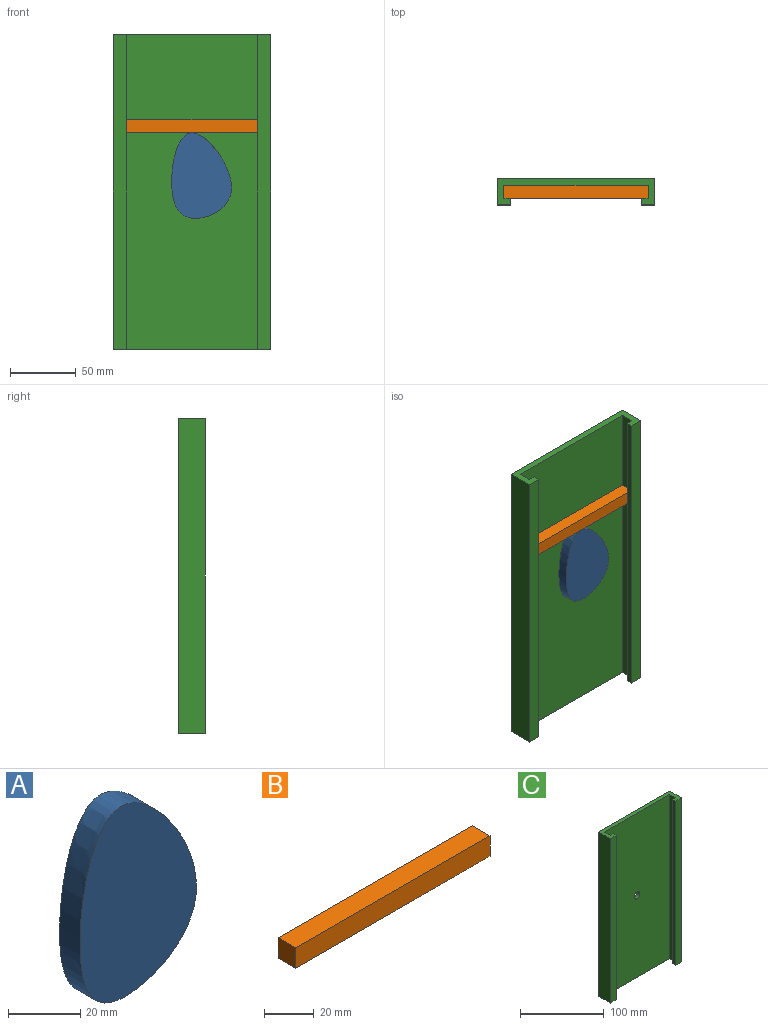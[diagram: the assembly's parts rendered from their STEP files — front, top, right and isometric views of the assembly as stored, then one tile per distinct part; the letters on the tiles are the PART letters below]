
ASSEMBLY  parts=3 mates=2
PART A: 5 faces, bbox 51x15x69 mm
  f0: plane 10x10mm, normal (0,1,0), area 78.5mm2, adj f1
  f1: cylinder r=5mm len=10mm, axis (0,-1,0), area 219.9mm2, adj f0,f4
  f2: extruded ~65.1x45.46mm, area 1405.8mm2, adj f3,f4
  f3: plane 69.02x51.05mm, normal (0,-1,0), area 2271.9mm2, adj f2
  f4: plane 69.02x51.05mm, normal (0,1,0), area 2193.4mm2, adj f1,f2
PART B: 6 faces, bbox 110x10x10 mm
  f0: plane 10x10mm, normal (1,0,0), area 100mm2, adj f1,f2,f4,f5
  f1: plane 110x10mm, normal (0,0,1), area 1100mm2, adj f0,f3,f4,f5
  f2: plane 110x10mm, normal (0,0,-1), area 1100mm2, adj f0,f3,f4,f5
  f3: plane 10x10mm, normal (-1,0,0), area 100mm2, adj f1,f2,f4,f5
  f4: plane 110x10mm, normal (0,1,0), area 1100mm2, adj f0,f1,f2,f3
  f5: plane 110x10mm, normal (0,-1,0), area 1100mm2, adj f0,f1,f2,f3
PART C: 15 faces, bbox 120x20x240 mm
  f0: plane 240x5mm, normal (1,0,0), area 1200mm2, adj f1,f3,f8,f13
  f1: plane 120x20mm, normal (0,0,-1), area 800mm2, adj f0,f2,f4,f5,f6,f7,f8,f9
  f2: plane 240x5mm, normal (-1,0,0), area 1200mm2, adj f1,f3,f6,f11
  f3: plane 120x20mm, normal (0,0,1), area 800mm2, adj f0,f2,f4,f5,f6,f7,f8,f9
  f4: plane 240x110mm, normal (0,-1,0), area 26321.5mm2, adj f1,f3,f5,f7,f14
  f5: plane 240x10mm, normal (-1,0,0), area 2400mm2, adj f1,f3,f4,f6
  f6: plane 240x5mm, normal (0,1,0), area 1200mm2, adj f1,f2,f3,f5
  f7: plane 240x10mm, normal (1,0,0), area 2400mm2, adj f1,f3,f4,f8
  f8: plane 240x5mm, normal (0,1,0), area 1200mm2, adj f0,f1,f3,f7
  f9: plane 240x120mm, normal (0,1,0), area 28721.5mm2, adj f1,f3,f10,f12,f14
  f10: plane 240x20mm, normal (1,0,0), area 4800mm2, adj f1,f3,f9,f11
  f11: plane 240x10mm, normal (0,-1,0), area 2400mm2, adj f1,f2,f3,f10
  f12: plane 240x20mm, normal (-1,0,0), area 4800mm2, adj f1,f3,f9,f13
  f13: plane 240x10mm, normal (0,-1,0), area 2400mm2, adj f0,f1,f3,f12
  f14: cylinder r=5mm len=10mm, axis (0,-1,0), area 157.1mm2, adj f4,f9
PLACE A rot(axis=(0,-1,0),1.1deg) t=(-136.98,53.47,-26.97)mm
PLACE B t=(-17,53.47,-89.53)mm
PLACE C t=(-17,53.47,-24.57)mm fixed
MATE revolute C.f14 <-> A.f1  axis (0,1,0) through (-17,60.47,-24.57)mm
MATE slider C.f3 <-> B.f1  axis (0,0,1) through (-72,55.47,95.43)mm
